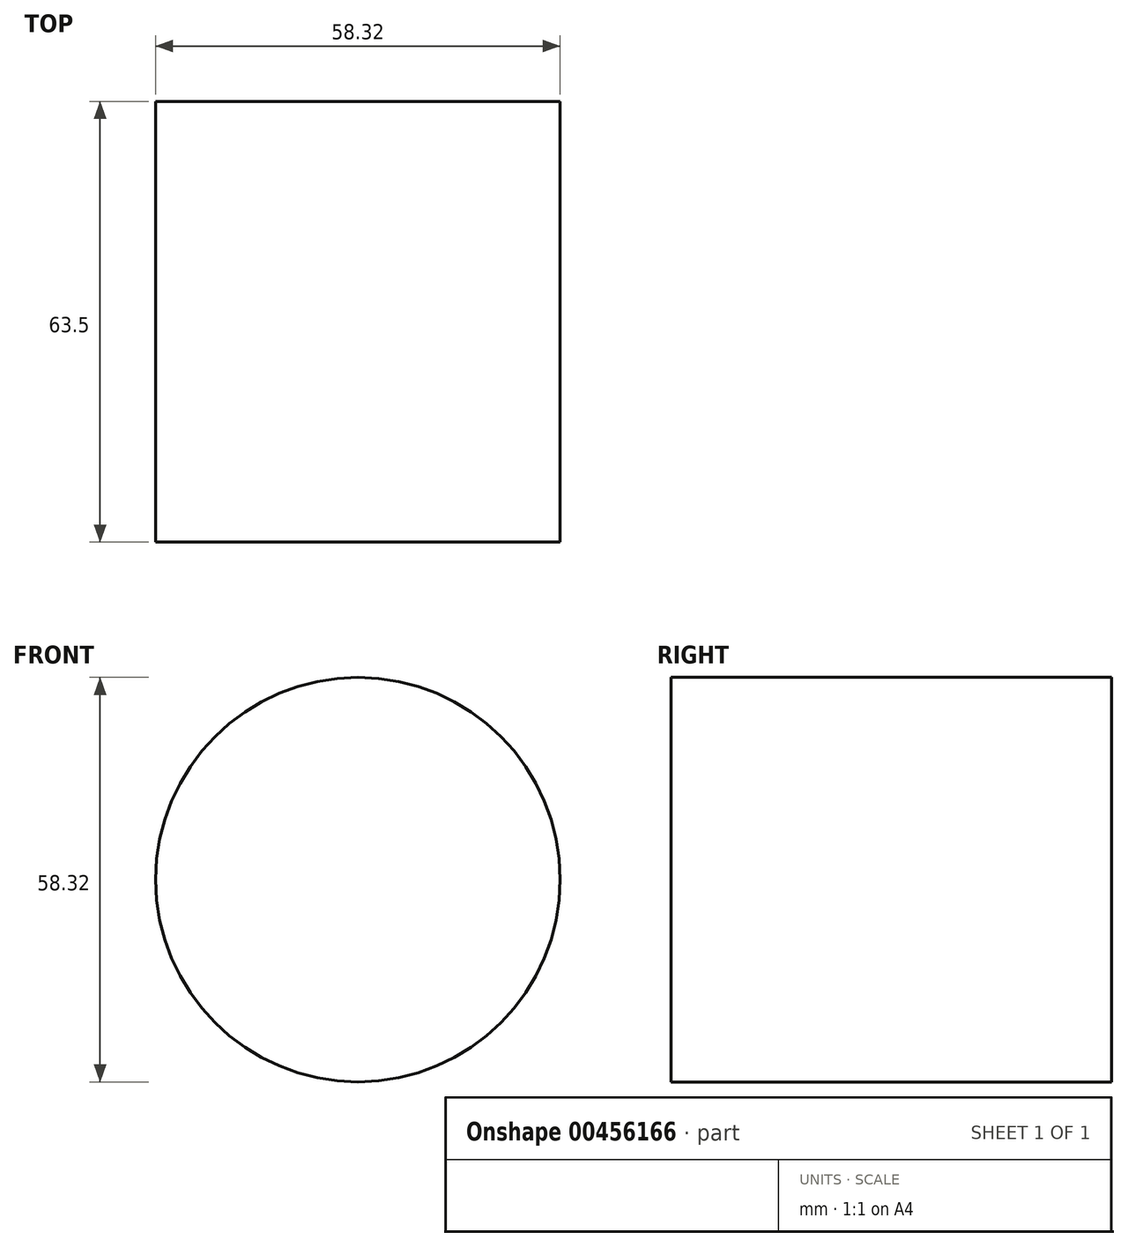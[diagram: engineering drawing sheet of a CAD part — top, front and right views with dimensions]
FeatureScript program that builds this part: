
annotation { "Feature Type Name" : "Feature", "Feature Type Description" : "" }
export const myFeature = defineFeature(function(context is Context, id is Id, definition is map)
    precondition{}
    {
        {
            var Q0;
            Q0=qCreatedBy(makeId("Front.planeOp"),FACE);
            var sketch = newSketch(context, id + "F0", { "sketchPlane" : qUnion([Q0])});
            skCircle(sketch, "E0", {"center": v(0, 0) * mm, "radius": 29.16 * mm});
            skSolve(sketch);
        }
        {
            var Q0;
            Q0 = qSketchRegion(id + "F0", true);
            extrude(context, id + "F1", {"entities" : qUnion([Q0]), "depth" : 63.5 * mm});
        }
    });
